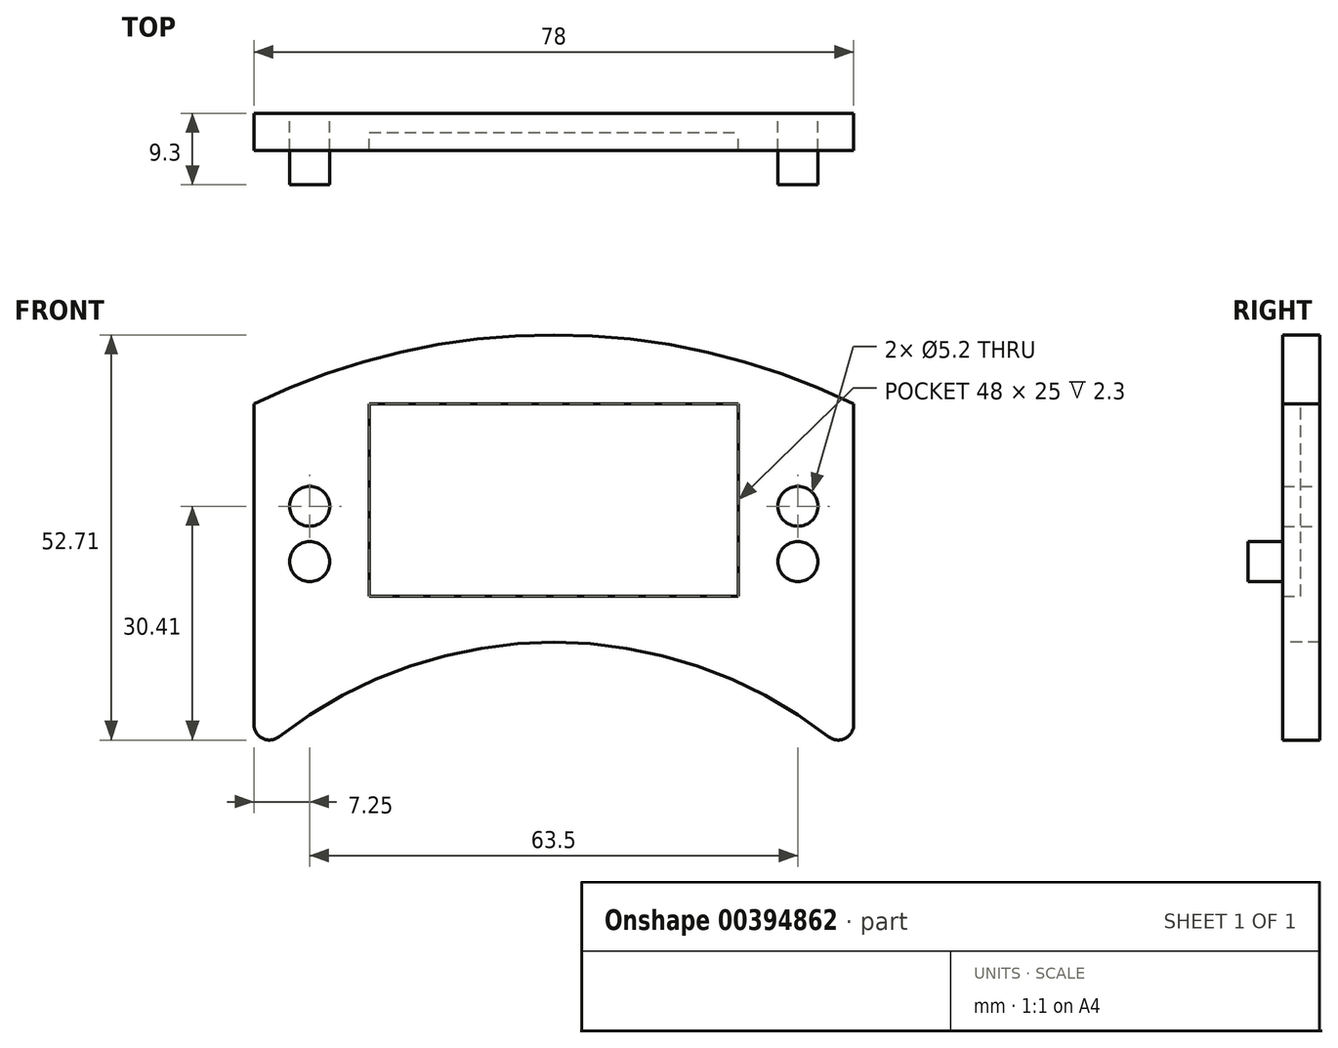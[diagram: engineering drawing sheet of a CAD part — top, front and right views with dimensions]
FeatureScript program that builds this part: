
annotation { "Feature Type Name" : "Feature", "Feature Type Description" : "" }
export const myFeature = defineFeature(function(context is Context, id is Id, definition is map)
    precondition{}
    {
        {
            var Q0;
            Q0=qCreatedBy(makeId("Front.planeOp"),FACE);
            var sketch = newSketch(context, id + "F0", { "sketchPlane" : qUnion([Q0])});
            skLineSegment(sketch, "E0", {"start": v(-39, -46) * mm, "end": v(-39, 0) * mm});
            skLineSegment(sketch, "E1", {"start": v(-39, 0) * mm, "end": v(39, 0) * mm, "construction": true});
            skLineSegment(sketch, "E2", {"start": v(39, 0) * mm, "end": v(39, -46) * mm});
            skArc(sketch, "E3", {"start": v(39, -46) * mm, "mid": v(0, -31) * mm, "end": v(-39, -46) * mm});
            skArc(sketch, "E4", {"start": v(39, 0) * mm, "mid": v(0, 9) * mm, "end": v(-39, 0) * mm});
            skSolve(sketch);
        }
        {
            var Q0;
            Q0=qSketchRegion(id+"F0",true);
            extrude(context, id + "F1", {"entities" : qUnion([Q0]), "oppositeDirection" : true, "depth" : 4.8 * mm});
        }
        {
            var Q0;
            Q0=makeQuery(id+"F1.opExtrude","CAP_FACE",FACE,{"disambiguationData":[OSD([sQuery(id+"F0.wireOp",EDGE,"E0"),sQuery(id+"F0.wireOp",EDGE,"E2"),sQuery(id+"F0.wireOp",EDGE,"E3"),sQuery(id+"F0.wireOp",EDGE,"E4")])],"isStart":true});
            var sketch = newSketch(context, id + "F2", { "sketchPlane" : qUnion([Q0])});
            skCircle(sketch, "E5", {"center": v(-31.75, -20.5) * mm, "radius": 2.6 * mm});
            skCircle(sketch, "E6", {"center": v(31.75, -20.5) * mm, "radius": 2.6 * mm});
            skSolve(sketch);
        }
        {
            var Q0;
            Q0=qSketchRegion(id+"F2",true);
            extrude(context, id + "F3", {"entities" : qUnion([Q0]), "operationType" : NewBodyOperationType.ADD, "depth" : 4.5 * mm});
        }
        {
            var Q0;
            Q0=makeQuery(id+"F1.opExtrude","CAP_FACE",FACE,{"disambiguationData":[OSD([sQuery(id+"F0.wireOp",EDGE,"E0"),sQuery(id+"F0.wireOp",EDGE,"E2"),sQuery(id+"F0.wireOp",EDGE,"E3"),sQuery(id+"F0.wireOp",EDGE,"E4")])],"isStart":false});
            var sketch = newSketch(context, id + "F4", { "sketchPlane" : qUnion([Q0])});
            skPoint(sketch, "E7", {"position": v(-31.75, -20.5) * mm});
            skPoint(sketch, "E8", {"position": v(31.75, -20.5) * mm});
            skCircle(sketch, "E9", {"center": v(-31.75, -20.5) * mm, "radius": 2.6 * mm, "construction": true});
            skCircle(sketch, "E10", {"center": v(31.75, -20.5) * mm, "radius": 2.6 * mm, "construction": true});
            skCircle(sketch, "E11", {"center": v(-31.75, -13.3) * mm, "radius": 2.6 * mm});
            skCircle(sketch, "E12", {"center": v(31.75, -13.3) * mm, "radius": 2.6 * mm});
            skSolve(sketch);
        }
        {
            var Q0;
            Q0=qSketchRegion(id+"F4",true);
            extrude(context, id + "F5", {"entities" : qUnion([Q0]), "operationType" : NewBodyOperationType.REMOVE, "endBound" : BoundingType.UP_TO_NEXT, "oppositeDirection" : true, "depth" : 2.2 * mm});
        }
        {
            var Q0;
            Q0=makeQuery(id+"F1.opExtrude","SWEPT_EDGE",EDGE,{"disambiguationData":[OSD([sQuery(id+"F0.wireOp",EDGE,"E0"),sQuery(id+"F0.wireOp",EDGE,"E3")])]});
            var Q1;
            Q1=makeQuery(id+"F1.opExtrude","SWEPT_EDGE",EDGE,{"disambiguationData":[OSD([sQuery(id+"F0.wireOp",EDGE,"E2"),sQuery(id+"F0.wireOp",EDGE,"E3")])]});
            fillet(context, id + "F6", {"entities" : qUnion([Q0, Q1]), "radius" : 2 * mm, "tangentPropagation" : true, "allowEdgeOverflow" : false});
        }
        {
            var Q0;
            Q0=qCreatedBy(makeId("Top.planeOp"),FACE);
            var sketch = newSketch(context, id + "F7", { "sketchPlane" : qUnion([Q0])});
            skLineSegment(sketch, "E13.bottom", {"start": v(-24, 0) * mm, "end": v(24, 0) * mm});
            skLineSegment(sketch, "E13.top", {"start": v(-24, 2.3) * mm, "end": v(24, 2.3) * mm});
            skLineSegment(sketch, "E13.left", {"start": v(-24, 0) * mm, "end": v(-24, 2.3) * mm});
            skLineSegment(sketch, "E13.right", {"start": v(24, 0) * mm, "end": v(24, 2.3) * mm});
            skSolve(sketch);
        }
        {
            var Q0;
            Q0=qSketchRegion(id+"F7",true);
            extrude(context, id + "F8", {"entities" : qUnion([Q0]), "operationType" : NewBodyOperationType.REMOVE, "oppositeDirection" : true, "depth" : 25 * mm});
        }
    });
